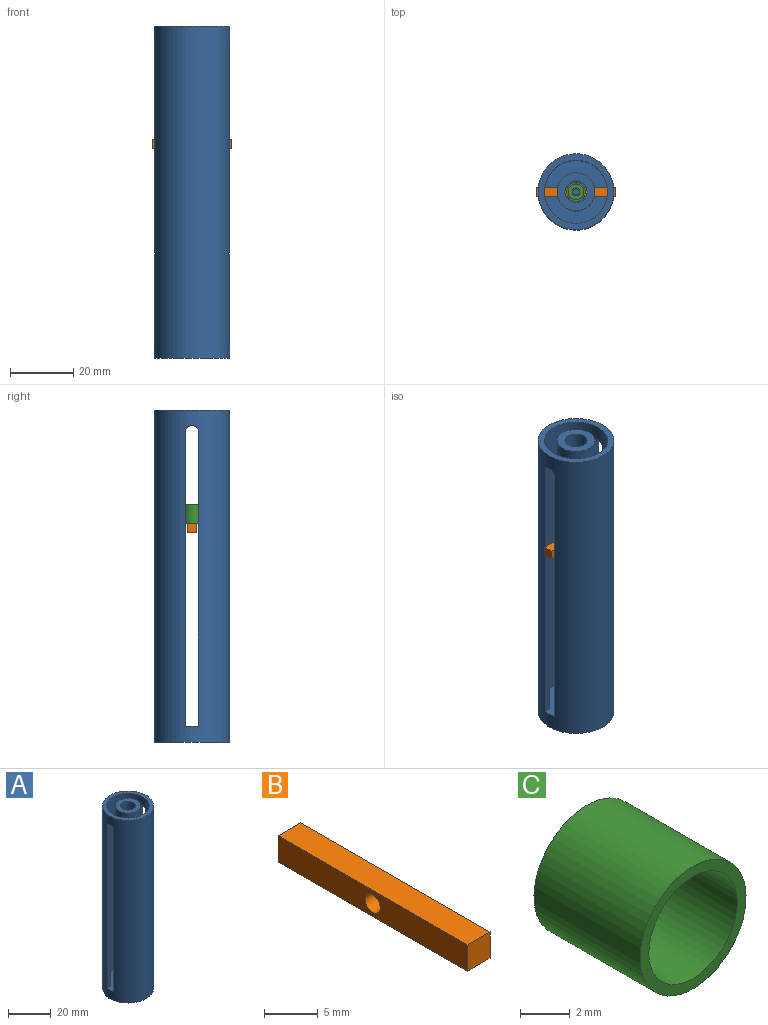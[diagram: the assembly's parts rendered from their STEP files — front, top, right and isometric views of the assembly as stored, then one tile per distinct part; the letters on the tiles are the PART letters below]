
ASSEMBLY  parts=3 mates=2
PART A: 28 faces, bbox 24x24x105 mm
  f0: cylinder r=3.5mm len=100mm, axis (0,0,-1), area 1392.4mm2, adj f4,f5,f14,f15,f16,f17,f18,f19
  f1: cylinder r=6mm len=100mm, axis (0,0,-1), area 2997.1mm2, adj f4,f5,f14,f15,f16,f17,f18,f19
  f2: cylinder r=10mm len=100mm, axis (0,0,-1), area 5520mm2, adj f5,f6,f8,f9,f10,f11,f12,f13
  f3: cylinder r=12mm len=105mm, axis (0,0,1), area 7155.2mm2, adj f5,f6,f7,f8,f9,f10,f11,f12
  f4: plane 12x12mm, normal (0,0,1), area 74.6mm2, adj f0,f1
  f5: plane 24x20mm, normal (0,0,1), area 276.3mm2, adj f0,f1,f2,f3,f9,f10,f12,f13
  f6: plane 24x24mm, normal (0,0,1), area 138.2mm2, adj f2,f3
  f7: plane 24x24mm, normal (0,0,-1), area 452.4mm2, adj f3
  f8: plane 2.01x1mm, normal (0,0,-1), area 2mm2, adj f2,f3,f26,f27
  f9: plane 93.5x2.03mm, normal (0,-1,0), area 190.2mm2, adj f2,f3,f5,f26
  f10: plane 93.5x2.03mm, normal (0,1,0), area 190.2mm2, adj f2,f3,f5,f27
  f11: plane 2.01x1mm, normal (0,0,-1), area 2mm2, adj f2,f3,f20,f23
  f12: plane 93.5x2.03mm, normal (0,-1,0), area 190.2mm2, adj f2,f3,f5,f23
  f13: plane 93.5x2.03mm, normal (0,1,0), area 190.2mm2, adj f2,f3,f5,f20
  f14: plane 2.54x1mm, normal (0,0,-1), area 2.5mm2, adj f0,f1,f22,f25
  f15: plane 93.5x2.78mm, normal (0,-1,0), area 260.4mm2, adj f0,f1,f5,f25
  f16: plane 93.5x2.78mm, normal (0,1,0), area 260.4mm2, adj f0,f1,f5,f22
  f17: plane 93.5x2.78mm, normal (0,1,0), area 260.4mm2, adj f0,f1,f5,f21
  f18: plane 93.5x2.78mm, normal (0,-1,0), area 260.4mm2, adj f0,f1,f5,f24
  f19: plane 2.54x1mm, normal (0,0,-1), area 2.5mm2, adj f0,f1,f21,f24
  f20: cylinder r=1.5mm len=2.19mm, axis (-1,0,0), area 4.8mm2, adj f2,f3,f11,f13
  f21: cylinder r=1.5mm len=3.11mm, axis (-1,0,0), area 6.3mm2, adj f0,f1,f17,f19
  f22: cylinder r=1.5mm len=3.11mm, axis (-1,0,0), area 6.3mm2, adj f0,f1,f14,f16
  f23: cylinder r=1.5mm len=2.19mm, axis (1,0,0), area 4.8mm2, adj f2,f3,f11,f12
  f24: cylinder r=1.5mm len=3.11mm, axis (1,0,0), area 6.3mm2, adj f0,f1,f18,f19
  f25: cylinder r=1.5mm len=3.11mm, axis (1,0,0), area 6.3mm2, adj f0,f1,f14,f15
  f26: cylinder r=1.5mm len=2.19mm, axis (1,0,0), area 4.8mm2, adj f2,f3,f8,f9
  f27: cylinder r=1.5mm len=2.19mm, axis (-1,0,0), area 4.8mm2, adj f2,f3,f8,f10
PART B: 7 faces, bbox 3x25x3 mm
  f0: plane 25x3mm, normal (1,0,0), area 71.9mm2, adj f1,f3,f4,f5,f6
  f1: plane 25x3mm, normal (0,0,1), area 75mm2, adj f0,f2,f4,f5
  f2: plane 25x3mm, normal (-1,0,0), area 71.9mm2, adj f1,f3,f4,f5,f6
  f3: plane 25x3mm, normal (0,0,-1), area 75mm2, adj f0,f2,f4,f5
  f4: plane 3x3mm, normal (0,-1,0), area 9mm2, adj f0,f1,f2,f3
  f5: plane 3x3mm, normal (0,1,0), area 9mm2, adj f0,f1,f2,f3
  f6: cylinder r=1mm len=3mm, axis (1,0,0), area 18.8mm2, adj f0,f2
PART C: 6 faces, bbox 6x6x6 mm
  f0: cylinder r=3mm len=6mm, axis (0,1,0), area 113.1mm2, adj f1,f2
  f1: plane 6x6mm, normal (0,-1,0), area 8.6mm2, adj f0,f3
  f2: plane 6x6mm, normal (0,1,0), area 23.4mm2, adj f0,f5
  f3: cylinder r=2.5mm len=5mm, axis (0,1,0), area 78.5mm2, adj f1,f4
  f4: plane 5x5mm, normal (0,-1,0), area 14.7mm2, adj f3,f5
  f5: cylinder r=1.25mm len=2.5mm, axis (0,1,0), area 7.9mm2, adj f2,f4
PLACE A t=(14.74,0,17.59)mm fixed
PLACE B rot(axis=(0.58,0.58,-0.58),120deg) t=(14.74,0,30.2)mm
PLACE C rot(axis=(-1,0,0),90deg) t=(14.74,0,30.2)mm
MATE fastened C.f0 <-> B.f6  axis (0,0,-1) through (14.74,0,31.7)mm
MATE slider C.f0 <-> A.f1  axis (0,0,1) through (14.74,0,37.7)mm
